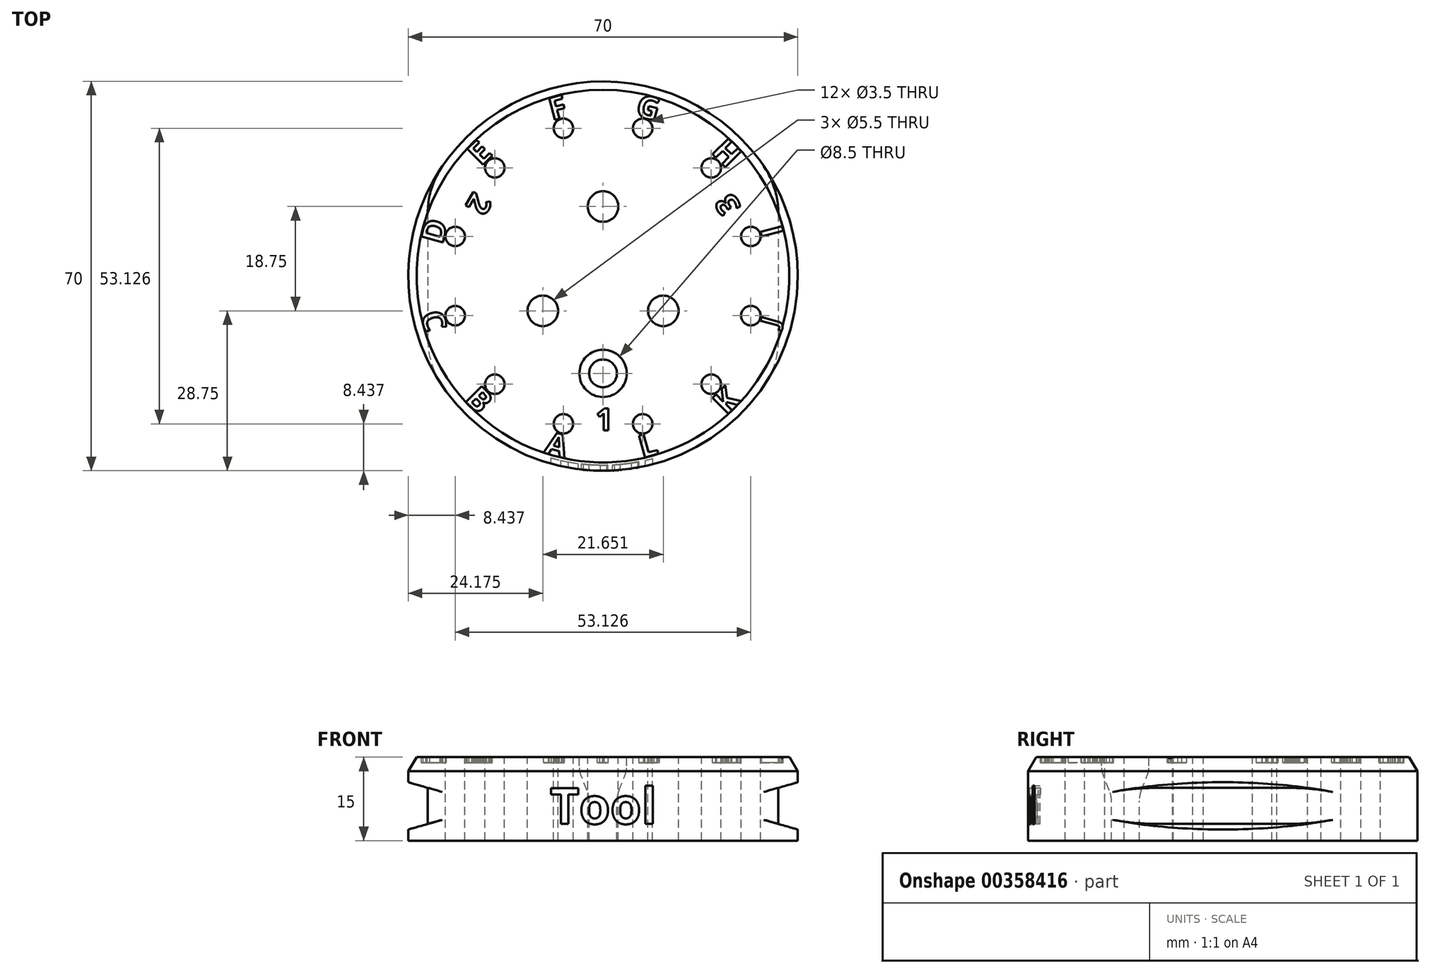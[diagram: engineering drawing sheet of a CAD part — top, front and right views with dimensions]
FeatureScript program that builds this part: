
annotation { "Feature Type Name" : "Feature", "Feature Type Description" : "" }
export const myFeature = defineFeature(function(context is Context, id is Id, definition is map)
    precondition{}
    {
        {
            var Q0;
            Q0=qCreatedBy(makeId("Top.planeOp"),FACE);
            var sketch = newSketch(context, id + "F0", { "sketchPlane" : qUnion([Q0])});
            skCircle(sketch, "E0", {"center": v(0, 0) * mm, "radius": 35 * mm});
            skSolve(sketch);
        }
        {
            var Q0;
            Q0=qSketchRegion(id+"F0",true);
            extrude(context, id + "F1", {"entities" : qUnion([Q0]), "depth" : 15 * mm});
        }
        {
            var Q0;
            Q0=qCreatedBy(makeId("Front.planeOp"),FACE);
            var sketch = newSketch(context, id + "F2", { "sketchPlane" : qUnion([Q0])});
            skText(sketch, "E1", { "text": "Tool", "fontName": "OpenSans-Bold.ttf"});
            const initialGuessF2  = {"E1": [-0.00952, 0.003, 1, 0, 0.0065]};
            skSetInitialGuess(sketch, initialGuessF2);
            skSolve(sketch);
        }
        {
            var Q0;
            Q0=qSketchRegion(id+"F2",true);
            var Q1;
            Q1=makeQuery(id+"F1.opExtrude","SWEPT_FACE",FACE,{"disambiguationData":[OSD([sQuery(id+"F0.wireOp",EDGE,"E0")])]});
            extrude(context, id + "F3", {"entities" : qUnion([Q0]), "operationType" : NewBodyOperationType.REMOVE, "endBound" : BoundingType.THROUGH_ALL, "endBoundEntityFace" : qUnion([Q1]), "depth" : 25 * mm});
        }
        {
            var Q0;
            Q0=makeQuery(id+"F1.opExtrude","CAP_FACE",FACE,{"disambiguationData":[OSD([sQuery(id+"F0.wireOp",EDGE,"E0")])],"isStart":false});
            var sketch = newSketch(context, id + "F4", { "sketchPlane" : qUnion([Q0])});
            skCircle(sketch, "E2", {"center": v(0, 0) * mm, "radius": 34 * mm});
            skSolve(sketch);
        }
        {
            var Q0;
            Q0=qSketchRegion(id+"F4",true);
            var Q1;
            Q1=makeQuery(id+"F1.opExtrude","CAP_FACE",FACE,{"disambiguationData":[OSD([sQuery(id+"F0.wireOp",EDGE,"E0")])],"isStart":true});
            extrude(context, id + "F5", {"entities" : qUnion([Q0]), "operationType" : NewBodyOperationType.ADD, "endBound" : BoundingType.UP_TO_SURFACE, "oppositeDirection" : true, "endBoundEntityFace" : qUnion([Q1]), "depth" : 25 * mm});
        }
        {
            var Q0;
            Q0=qCreatedBy(makeId("Front.planeOp"),FACE);
            var sketch = newSketch(context, id + "F6", { "sketchPlane" : qUnion([Q0])});
            skLineSegment(sketch, "E3", {"start": v(-35, 10.5) * mm, "end": v(-35, 2) * mm});
            skLineSegment(sketch, "E4", {"start": v(-35, 2) * mm, "end": v(-31.5, 3) * mm});
            skLineSegment(sketch, "E5", {"start": v(-31.5, 3) * mm, "end": v(-31.5, 9.5) * mm});
            skLineSegment(sketch, "E6", {"start": v(-31.5, 9.5) * mm, "end": v(-35, 10.5) * mm});
            skLineSegment(sketch, "E7.MirrorCS", {"start": v(35, 10.5) * mm, "end": v(35, 2) * mm});
            skLineSegment(sketch, "E8.MirrorCS", {"start": v(31.5, 9.5) * mm, "end": v(35, 10.5) * mm});
            skLineSegment(sketch, "E9.MirrorCS", {"start": v(35, 2) * mm, "end": v(31.5, 3) * mm});
            skLineSegment(sketch, "E10.MirrorCS", {"start": v(31.5, 3) * mm, "end": v(31.5, 9.5) * mm});
            skSolve(sketch);
        }
        {
            var Q0;
            Q0=qSketchRegion(id+"F6",true);
            extrude(context, id + "F7", {"entities" : qUnion([Q0]), "operationType" : NewBodyOperationType.REMOVE, "endBound" : BoundingType.THROUGH_ALL, "oppositeDirection" : true, "depth" : 25 * mm, "hasSecondDirection" : true, "secondDirectionBound" : BoundingType.THROUGH_ALL, "secondDirectionOppositeDirection" : false, "secondDirectionDepth" : 25 * mm});
        }
        {
            var Q0;
            {var subQ0=sQuery(id+"F0.wireOp",EDGE,"E0");Q0=makeQuery(id+"F7.boolean.opBoolean","INTERSECT",EDGE,{"disambiguationData":[OD(0.0)],"derivedFrom":[makeQuery(id+"F3.boolean.opBoolean","SPLIT",FACE,{"disambiguationData":[TD([makeQuery(id+"F1.opExtrude","CAP_FACE",FACE,{"disambiguationData":[OSD([subQ0])],"isStart":true})])],"derivedFrom":makeQuery(id+"F1.opExtrude","SWEPT_FACE",FACE,{"disambiguationData":[OSD([subQ0])]})}),makeQuery(id+"F7.opExtrude","SWEPT_FACE",FACE,{"disambiguationData":[OSD([sQuery(id+"F6.wireOp",EDGE,"E5")])]})]});}
            var Q1;
            {var subQ0=sQuery(id+"F0.wireOp",EDGE,"E0");Q1=makeQuery(id+"F7.boolean.opBoolean","INTERSECT",EDGE,{"disambiguationData":[OD(0.0)],"derivedFrom":[makeQuery(id+"F3.boolean.opBoolean","SPLIT",FACE,{"disambiguationData":[TD([makeQuery(id+"F1.opExtrude","CAP_FACE",FACE,{"disambiguationData":[OSD([subQ0])],"isStart":true})])],"derivedFrom":makeQuery(id+"F1.opExtrude","SWEPT_FACE",FACE,{"disambiguationData":[OSD([subQ0])]})}),makeQuery(id+"F7.opExtrude","SWEPT_FACE",FACE,{"disambiguationData":[OSD([sQuery(id+"F6.wireOp",EDGE,"E10.MirrorCS")])]})]});}
            var Q2;
            {var subQ0=sQuery(id+"F0.wireOp",EDGE,"E0");Q2=makeQuery(id+"F7.boolean.opBoolean","INTERSECT",EDGE,{"disambiguationData":[OD(1.0)],"derivedFrom":[makeQuery(id+"F3.boolean.opBoolean","SPLIT",FACE,{"disambiguationData":[TD([makeQuery(id+"F1.opExtrude","CAP_FACE",FACE,{"disambiguationData":[OSD([subQ0])],"isStart":true})])],"derivedFrom":makeQuery(id+"F1.opExtrude","SWEPT_FACE",FACE,{"disambiguationData":[OSD([subQ0])]})}),makeQuery(id+"F7.opExtrude","SWEPT_FACE",FACE,{"disambiguationData":[OSD([sQuery(id+"F6.wireOp",EDGE,"E10.MirrorCS")])]})]});}
            var Q3;
            {var subQ0=sQuery(id+"F0.wireOp",EDGE,"E0");Q3=makeQuery(id+"F7.boolean.opBoolean","INTERSECT",EDGE,{"disambiguationData":[OD(1.0)],"derivedFrom":[makeQuery(id+"F3.boolean.opBoolean","SPLIT",FACE,{"disambiguationData":[TD([makeQuery(id+"F1.opExtrude","CAP_FACE",FACE,{"disambiguationData":[OSD([subQ0])],"isStart":true})])],"derivedFrom":makeQuery(id+"F1.opExtrude","SWEPT_FACE",FACE,{"disambiguationData":[OSD([subQ0])]})}),makeQuery(id+"F7.opExtrude","SWEPT_FACE",FACE,{"disambiguationData":[OSD([sQuery(id+"F6.wireOp",EDGE,"E5")])]})]});}
            fillet(context, id + "F8", {"entities" : qUnion([Q0, Q1, Q2, Q3]), "radius" : 15 * mm, "tangentPropagation" : true, "allowEdgeOverflow" : false});
        }
        {
            var Q0;
            Q0=makeQuery(id+"F1.opExtrude","CAP_FACE",FACE,{"disambiguationData":[OSD([sQuery(id+"F0.wireOp",EDGE,"E0")])],"isStart":false});
            var sketch = newSketch(context, id + "F9", { "sketchPlane" : qUnion([Q0])});
            skCircle(sketch, "E11", {"center": v(0, 12.5) * mm, "radius": 2.75 * mm});
            skCircle(sketch, "E12.1.0", {"center": v(-10.83, -6.25) * mm, "radius": 2.75 * mm});
            skCircle(sketch, "E12.2.0", {"center": v(10.83, -6.25) * mm, "radius": 2.75 * mm});
            skPoint(sketch, "E12.center", {"position": v(0, 0) * mm});
            skCircle(sketch, "E13", {"center": v(0, 0) * mm, "radius": 12.5 * mm, "construction": true});
            skSolve(sketch);
        }
        {
            var Q0;
            Q0=qSketchRegion(id+"F9",true);
            extrude(context, id + "F10", {"entities" : qUnion([Q0]), "operationType" : NewBodyOperationType.REMOVE, "endBound" : BoundingType.THROUGH_ALL, "oppositeDirection" : true, "depth" : 25 * mm});
        }
        {
            var Q0;
            Q0=makeQuery(id+"F1.opExtrude","CAP_FACE",FACE,{"disambiguationData":[OSD([sQuery(id+"F0.wireOp",EDGE,"E0")])],"isStart":false});
            var sketch = newSketch(context, id + "F11", { "sketchPlane" : qUnion([Q0])});
            skCircle(sketch, "E14", {"center": v(0, -17.5) * mm, "radius": 2.5 * mm});
            skCircle(sketch, "E15", {"center": v(0, 0) * mm, "radius": 17.5 * mm, "construction": true});
            skSolve(sketch);
        }
        {
            var Q0;
            Q0=qSketchRegion(id+"F11",true);
            extrude(context, id + "F12", {"entities" : qUnion([Q0]), "operationType" : NewBodyOperationType.REMOVE, "endBound" : BoundingType.THROUGH_ALL, "oppositeDirection" : true, "depth" : 25 * mm});
        }
        {
            var Q0;
            Q0=makeQuery(id+"F1.opExtrude","CAP_FACE",FACE,{"disambiguationData":[OSD([sQuery(id+"F0.wireOp",EDGE,"E0")])],"isStart":false});
            var sketch = newSketch(context, id + "F13", { "sketchPlane" : qUnion([Q0])});
            skCircle(sketch, "E16", {"center": v(0, -17.5) * mm, "radius": 4.25 * mm});
            skSolve(sketch);
        }
        {
            var Q0;
            Q0=qSketchRegion(id+"F13",true);
            extrude(context, id + "F14", {"entities" : qUnion([Q0]), "operationType" : NewBodyOperationType.REMOVE, "oppositeDirection" : true, "depth" : 7.5 * mm});
        }
        {
            var Q0;
            Q0=makeQuery(id+"F14.boolean.opBoolean","COPY",EDGE,{"derivedFrom":makeQuery(id+"F14.opExtrude","CAP_EDGE",EDGE,{"disambiguationData":[OSD([sQuery(id+"F13.wireOp",EDGE,"E16")])],"isStart":false})});
            chamfer(context, id + "F15", {"entities" : qUnion([Q0]), "chamferType" : ChamferType.TWO_OFFSETS, "width1" : 5 * mm, "oppositeDirection" : true, "width2" : 2 * mm, "tangentPropagation" : true});
        }
        {
            var Q0;
            {var subQ0=sQuery(id+"F13.wireOp",EDGE,"E16");Q0=makeQuery(id+"F15.opChamfer","BLEND_EDGE",EDGE,{"blendedFrom":[makeQuery(id+"F14.boolean.opBoolean","COPY",EDGE,{"derivedFrom":makeQuery(id+"F14.opExtrude","CAP_EDGE",EDGE,{"disambiguationData":[OSD([subQ0])],"isStart":false})}),makeQuery(id+"F14.boolean.opBoolean","COPY",FACE,{"derivedFrom":makeQuery(id+"F14.opExtrude","SWEPT_FACE",FACE,{"disambiguationData":[OSD([subQ0])]})})],"blendedInto":[makeQuery(id+"F14.boolean.opBoolean","COPY",FACE,{"derivedFrom":makeQuery(id+"F14.opExtrude","SWEPT_FACE",FACE,{"disambiguationData":[OSD([subQ0])]})})]});}
            var Q1;
            Q1=makeQuery(id+"F15.opChamfer","BLEND_EDGE",EDGE,{"blendedFrom":[makeQuery(id+"F14.boolean.opBoolean","COPY",EDGE,{"derivedFrom":makeQuery(id+"F14.opExtrude","CAP_EDGE",EDGE,{"disambiguationData":[OSD([sQuery(id+"F13.wireOp",EDGE,"E16")])],"isStart":false})}),makeQuery(id+"F12.boolean.opBoolean","COPY",FACE,{"derivedFrom":makeQuery(id+"F12.opExtrude","SWEPT_FACE",FACE,{"disambiguationData":[OSD([sQuery(id+"F11.wireOp",EDGE,"E14")])]})})],"blendedInto":[makeQuery(id+"F12.boolean.opBoolean","COPY",FACE,{"derivedFrom":makeQuery(id+"F12.opExtrude","SWEPT_FACE",FACE,{"disambiguationData":[OSD([sQuery(id+"F11.wireOp",EDGE,"E14")])]})})]});
            fillet(context, id + "F16", {"entities" : qUnion([Q0, Q1]), "radius" : 5 * mm, "tangentPropagation" : true, "allowEdgeOverflow" : false});
        }
        {
            var Q0;
            Q0=makeQuery(id+"F1.opExtrude","CAP_FACE",FACE,{"disambiguationData":[OSD([sQuery(id+"F0.wireOp",EDGE,"E0")])],"isStart":false});
            var sketch = newSketch(context, id + "F17", { "sketchPlane" : qUnion([Q0])});
            skCircle(sketch, "E17", {"center": v(19.45, 19.45) * mm, "radius": 1.75 * mm});
            skCircle(sketch, "E18", {"center": v(0, 0) * mm, "radius": 27.5 * mm, "construction": true});
            skLineSegment(sketch, "E19", {"start": v(0, 0) * mm, "end": v(19.45, 19.45) * mm, "construction": true});
            skCircle(sketch, "E20.1.1", {"center": v(7.12, 26.56) * mm, "radius": 1.75 * mm});
            skCircle(sketch, "E20.2.1", {"center": v(-7.12, 26.56) * mm, "radius": 1.75 * mm});
            skCircle(sketch, "E20.3.1", {"center": v(-19.45, 19.45) * mm, "radius": 1.75 * mm});
            skCircle(sketch, "E20.4.1", {"center": v(-26.56, 7.12) * mm, "radius": 1.75 * mm});
            skCircle(sketch, "E20.5.1", {"center": v(-26.56, -7.12) * mm, "radius": 1.75 * mm});
            skCircle(sketch, "E20.6.1", {"center": v(-19.45, -19.45) * mm, "radius": 1.75 * mm});
            skCircle(sketch, "E20.7.1", {"center": v(-7.12, -26.56) * mm, "radius": 1.75 * mm});
            skCircle(sketch, "E20.8.1", {"center": v(7.12, -26.56) * mm, "radius": 1.75 * mm});
            skCircle(sketch, "E20.9.1", {"center": v(19.45, -19.45) * mm, "radius": 1.75 * mm});
            skCircle(sketch, "E20.10.1", {"center": v(26.56, -7.12) * mm, "radius": 1.75 * mm});
            skCircle(sketch, "E20.11.1", {"center": v(26.56, 7.12) * mm, "radius": 1.75 * mm});
            skSolve(sketch);
        }
        {
            var Q0;
            Q0=qSketchRegion(id+"F17",true);
            extrude(context, id + "F18", {"entities" : qUnion([Q0]), "operationType" : NewBodyOperationType.REMOVE, "endBound" : BoundingType.THROUGH_ALL, "oppositeDirection" : true, "depth" : 25 * mm});
        }
        {
            var Q0;
            Q0=makeQuery(id+"F1.opExtrude","CAP_EDGE",EDGE,{"disambiguationData":[OSD([sQuery(id+"F0.wireOp",EDGE,"E0")])],"isStart":false});
            chamfer(context, id + "F19", {"entities" : qUnion([Q0]), "chamferType" : ChamferType.TWO_OFFSETS, "width1" : 2.5 * mm, "oppositeDirection" : true, "width2" : 1.5 * mm, "tangentPropagation" : true});
        }
        {
            var Q0;
            Q0=makeQuery(id+"F1.opExtrude","CAP_FACE",FACE,{"disambiguationData":[OSD([sQuery(id+"F0.wireOp",EDGE,"E0")])],"isStart":false});
            var sketch = newSketch(context, id + "F20", { "sketchPlane" : qUnion([Q0])});
            skText(sketch, "E21", { "text": "A", "fontName": "OpenSans-Bold.ttf"});
            skText(sketch, "E22", { "text": "B", "fontName": "OpenSans-Bold.ttf"});
            skText(sketch, "E23", { "text": "C", "fontName": "OpenSans-Bold.ttf"});
            skText(sketch, "E24", { "text": "E", "fontName": "OpenSans-Bold.ttf"});
            skText(sketch, "E25", { "text": "F", "fontName": "OpenSans-Bold.ttf"});
            skText(sketch, "E26", { "text": "G", "fontName": "OpenSans-Bold.ttf"});
            skText(sketch, "E27", { "text": "H", "fontName": "OpenSans-Bold.ttf"});
            skText(sketch, "E28", { "text": "I", "fontName": "OpenSans-Bold.ttf"});
            skText(sketch, "E29", { "text": "J", "fontName": "OpenSans-Bold.ttf"});
            skText(sketch, "E30", { "text": "K", "fontName": "OpenSans-Bold.ttf"});
            skText(sketch, "E31", { "text": "L", "fontName": "OpenSans-Bold.ttf"});
            skText(sketch, "E32", { "text": "D", "fontName": "OpenSans-Bold.ttf"});
            skCircle(sketch, "E33", {"center": v(0, 0) * mm, "radius": 29.38 * mm, "construction": true});
            skText(sketch, "E34", { "text": "1", "fontName": "OpenSans-Bold.ttf"});
            skText(sketch, "E35", { "text": "2", "fontName": "OpenSans-Bold.ttf"});
            skText(sketch, "E36", { "text": "3", "fontName": "OpenSans-Bold.ttf"});
            skCircle(sketch, "E37", {"center": v(0, 0) * mm, "radius": 23.75 * mm, "construction": true});
            const initialGuessF20  = {"E21": [-0.0107, -0.03174, 0.96593, -0.25882, 0.00406], "E22": [-0.025, -0.02228, 0.7071, -0.7071, 0.00406], "E23": [-0.03278, -0.00684, 0.25882, -0.96593, 0.00406], "E24": [-0.0219, 0.01964, 0.7071, 0.7071, 0.00406], "E25": [-0.00914, 0.02796, 0.96593, 0.25882, 0.00406], "E26": [0.00567, 0.0289, 0.96593, -0.25882, 0.00406], "E27": [0.0193, 0.02225, 0.7071, -0.7071, 0.00406], "E28": [0.02815, 0.00844, 0.25882, -0.96593, 0.00406], "E29": [0.0313, -0.00927, 0.25882, 0.96593, 0.00325], "E30": [0.02219, -0.0251, 0.7071, 0.7071, 0.00406], "E31": [0.00703, -0.03273, 0.96593, 0.25882, 0.00406], "E32": [-0.02892, 0.00557, 0.25882, 0.96593, 0.00406], "E34": [-0.00133, -0.02775, 1, 0, 0.004], "E35": [-0.0232, 0.01533, -0.5, -0.86603, 0.004], "E36": [0.02486, 0.01244, -0.5, 0.86603, 0.004]};
            skSetInitialGuess(sketch, initialGuessF20);
            skSolve(sketch);
        }
        {
            var Q0;
            Q0=qSketchRegion(id+"F20",true);
            extrude(context, id + "F21", {"entities" : qUnion([Q0]), "operationType" : NewBodyOperationType.REMOVE, "oppositeDirection" : true, "depth" : 1 * mm});
        }
    });
